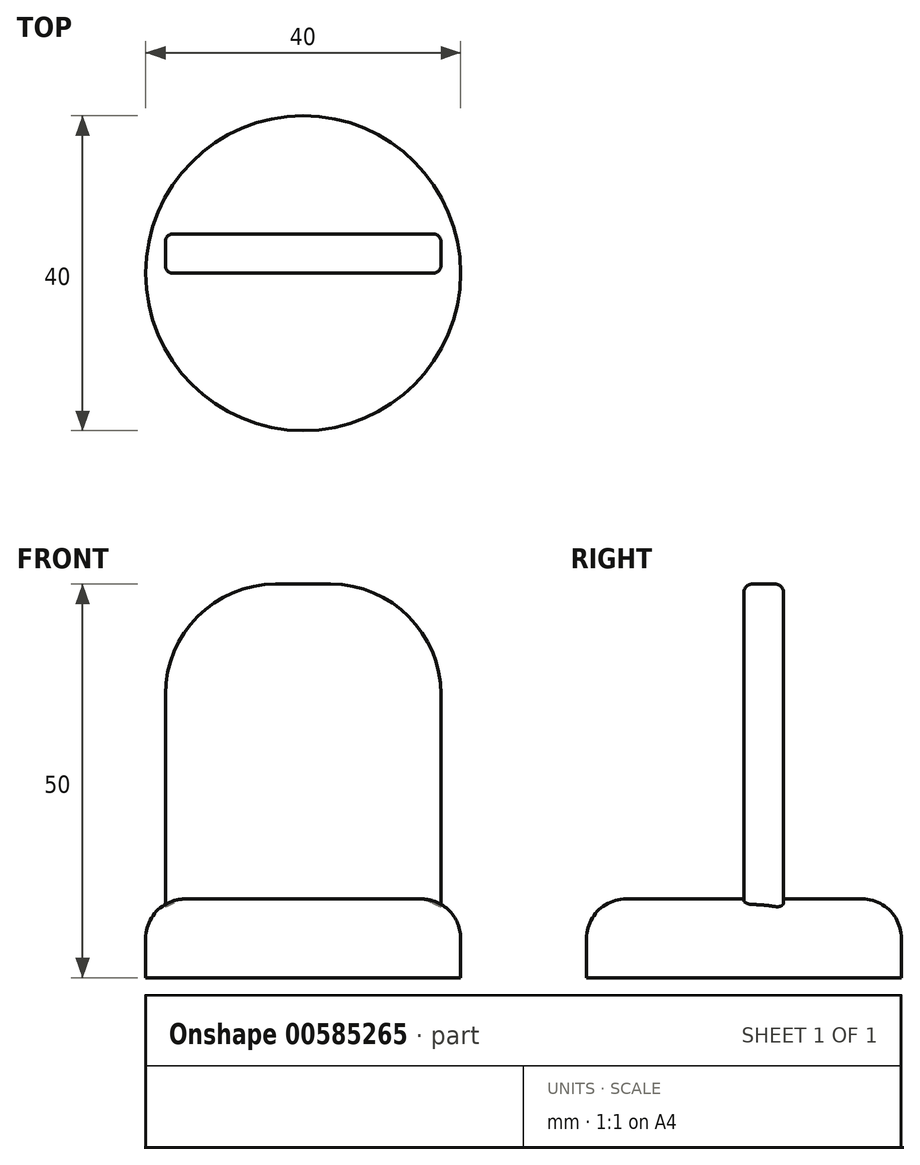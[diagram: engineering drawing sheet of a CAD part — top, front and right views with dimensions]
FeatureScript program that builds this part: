
annotation { "Feature Type Name" : "Feature", "Feature Type Description" : "" }
export const myFeature = defineFeature(function(context is Context, id is Id, definition is map)
    precondition{}
    {
        {
            var Q0;
            Q0=qCreatedBy(makeId("Top.planeOp"),FACE);
            var sketch = newSketch(context, id + "F0", { "sketchPlane" : qUnion([Q0])});
            skCircle(sketch, "E0", {"center": v(42.43, 38.54) * mm, "radius": 20 * mm});
            skLineSegment(sketch, "E1.top", {"start": v(24.93, 38.54) * mm, "end": v(59.93, 38.54) * mm});
            skLineSegment(sketch, "E1.left", {"start": v(24.93, 38.54) * mm, "end": v(24.93, 38.54) * mm});
            skLineSegment(sketch, "E1.right", {"start": v(59.93, 38.54) * mm, "end": v(59.93, 38.54) * mm});
            skLineSegment(sketch, "E2.top", {"start": v(24.93, 43.54) * mm, "end": v(59.93, 43.54) * mm});
            skLineSegment(sketch, "E2.left", {"start": v(24.93, 38.54) * mm, "end": v(24.93, 43.54) * mm});
            skLineSegment(sketch, "E2.right", {"start": v(59.93, 38.54) * mm, "end": v(59.93, 43.54) * mm});
            skSolve(sketch);
        }
        {
            var Q0;
            Q0=makeQuery(id+"F0.imprint","IMPRINT",FACE,{"disambiguationData":[TD([[makeQuery(id+"F0.imprint","IMPRINT",EDGE,{"derivedFrom":sQuery(id+"F0.wireOp",EDGE,"E0")}),1.0]])]});
            extrude(context, id + "F1", {"entities" : qUnion([Q0]), "depth" : 10 * mm, "offsetDistance" : 25 * mm});
        }
        {
            var Q0;
            Q0=makeQuery(id+"F0.imprint","IMPRINT",FACE,{"disambiguationData":[TD([[makeQuery(id+"F0.imprint","IMPRINT",EDGE,{"derivedFrom":sQuery(id+"F0.wireOp",EDGE,"E1.top")}),1.0]])]});
            extrude(context, id + "F2", {"entities" : qUnion([Q0]), "operationType" : NewBodyOperationType.ADD, "depth" : 50 * mm, "offsetDistance" : 25 * mm});
        }
        {
            var Q0;
            Q0=makeQuery(id+"F2.opExtrude","CAP_EDGE",EDGE,{"disambiguationData":[OSD([sQuery(id+"F0.wireOp",EDGE,"E1.top")])],"isStart":false});
            var Q1;
            Q1=makeQuery(id+"F2.opExtrude","SWEPT_EDGE",EDGE,{"disambiguationData":[OSD([sQuery(id+"F0.wireOp",EDGE,"E1.top"),sQuery(id+"F0.wireOp",EDGE,"E2.right")])]});
            var Q2;
            Q2=makeQuery(id+"F2.opExtrude","SWEPT_EDGE",EDGE,{"disambiguationData":[OSD([sQuery(id+"F0.wireOp",EDGE,"E1.top"),sQuery(id+"F0.wireOp",EDGE,"E2.left")])]});
            var Q3;
            Q3=makeQuery(id+"F2.opExtrude","SWEPT_EDGE",EDGE,{"disambiguationData":[OSD([sQuery(id+"F0.wireOp",EDGE,"E2.top"),sQuery(id+"F0.wireOp",EDGE,"E2.left")])]});
            var Q4;
            Q4=makeQuery(id+"F2.opExtrude","SWEPT_EDGE",EDGE,{"disambiguationData":[OSD([sQuery(id+"F0.wireOp",EDGE,"E2.top"),sQuery(id+"F0.wireOp",EDGE,"E2.right")])]});
            var Q5;
            Q5=makeQuery(id+"F2.opExtrude","CAP_EDGE",EDGE,{"disambiguationData":[OSD([sQuery(id+"F0.wireOp",EDGE,"E2.top")])],"isStart":false});
            fillet(context, id + "F3", {"entities" : qUnion([Q0, Q1, Q2, Q3, Q4, Q5]), "radius" : 1 * mm, "tangentPropagation" : true, "allowEdgeOverflow" : false});
        }
        {
            var Q0;
            Q0=makeQuery(id+"F1.opExtrude","CAP_EDGE",EDGE,{"disambiguationData":[OSD([sQuery(id+"F0.wireOp",EDGE,"E0")])],"isStart":false});
            fillet(context, id + "F4", {"entities" : qUnion([Q0]), "radius" : 5 * mm, "tangentPropagation" : true, "allowEdgeOverflow" : false});
        }
        {
            var Q0;
            Q0=makeQuery(id+"F2.opExtrude","CAP_EDGE",EDGE,{"disambiguationData":[OSD([sQuery(id+"F0.wireOp",EDGE,"E2.right")])],"isStart":false});
            var Q1;
            Q1=makeQuery(id+"F2.opExtrude","CAP_FACE",FACE,{"disambiguationData":[OSD([sQuery(id+"F0.wireOp",EDGE,"E1.top"),sQuery(id+"F0.wireOp",EDGE,"E2.top"),sQuery(id+"F0.wireOp",EDGE,"E2.left"),sQuery(id+"F0.wireOp",EDGE,"E2.right")])],"isStart":false});
            var Q2;
            Q2=makeQuery(id+"F1.opExtrude","CAP_EDGE",EDGE,{"disambiguationData":[OSD([sQuery(id+"F0.wireOp",EDGE,"E2.top")])],"isStart":false});
            var Q3;
            {var subQ0=sQuery(id+"F0.wireOp",EDGE,"E0");Q3=makeQuery(id+"F4.opFillet","BLEND_EDGE",EDGE,{"disambiguationData":[OD(1.0)],"blendedFrom":[makeQuery(id+"F1.opExtrude","CAP_EDGE",EDGE,{"disambiguationData":[OSD([subQ0])],"isStart":false}),makeQuery(id+"F1.opExtrude","CAP_FACE",FACE,{"disambiguationData":[OSD([subQ0,sQuery(id+"F0.wireOp",EDGE,"E1.top"),sQuery(id+"F0.wireOp",EDGE,"E2.top"),sQuery(id+"F0.wireOp",EDGE,"E2.left"),sQuery(id+"F0.wireOp",EDGE,"E2.right")])],"isStart":false})],"blendedInto":[makeQuery(id+"F1.opExtrude","CAP_FACE",FACE,{"disambiguationData":[OSD([subQ0,sQuery(id+"F0.wireOp",EDGE,"E1.top"),sQuery(id+"F0.wireOp",EDGE,"E2.top"),sQuery(id+"F0.wireOp",EDGE,"E2.left"),sQuery(id+"F0.wireOp",EDGE,"E2.right")])],"isStart":false})]});}
            fillet(context, id + "F5", {"entities" : qUnion([Q0, Q1, Q2, Q3]), "radius" : 14 * mm, "tangentPropagation" : true, "allowEdgeOverflow" : false});
        }
    });
